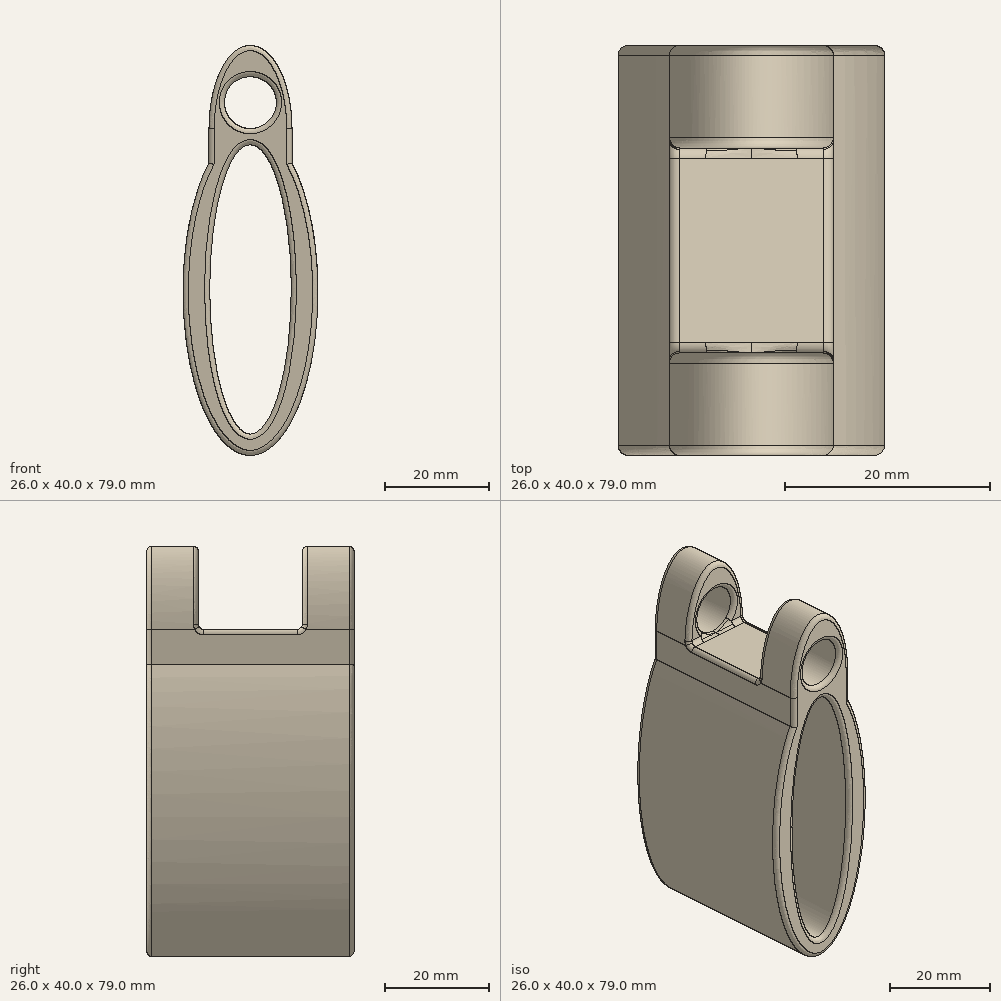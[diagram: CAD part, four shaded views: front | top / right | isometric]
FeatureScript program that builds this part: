
annotation { "Feature Type Name" : "Feature", "Feature Type Description" : "" }
export const myFeature = defineFeature(function(context is Context, id is Id, definition is map)
    precondition{}
    {
        {
            var Q0;
            Q0=qCreatedBy(makeId("Front.planeOp"),FACE);
            var sketch = newSketch(context, id + "F0", { "sketchPlane" : qUnion([Q0])});
            skEllipse(sketch, "E0", {"center": v(0, 0) * mm, "majorRadius": 28 * mm, "minorRadius": 8 * mm, "majorAxis": v(0, -1)});
            skLineSegment(sketch, "E1", {"start": v(0, 0) * mm, "end": v(8, 0) * mm, "construction": true});
            skLineSegment(sketch, "E2", {"start": v(0, 0) * mm, "end": v(0, 28) * mm, "construction": true});
            skLineSegment(sketch, "E3", {"start": v(-13, 0) * mm, "end": v(-8, 0) * mm, "construction": true});
            skLineSegment(sketch, "E4", {"start": v(0, 28) * mm, "end": v(0, 31) * mm, "construction": true});
            skLineSegment(sketch, "E5", {"start": v(0, 31) * mm, "end": v(0, 41) * mm, "construction": true});
            skPoint(sketch, "E6", {"position": v(0, 36) * mm});
            skCircle(sketch, "E7", {"center": v(0, 36) * mm, "radius": 5 * mm});
            skLineSegment(sketch, "E8", {"start": v(0, -28) * mm, "end": v(0, -32) * mm, "construction": true});
            skLineSegment(sketch, "E9.MirrorCS", {"start": v(8, 0) * mm, "end": v(8, 24.35) * mm, "construction": true});
            skPoint(sketch, "E10", {"position": v(0, 41) * mm});
            skLineSegment(sketch, "E11", {"start": v(0, 39) * mm, "end": v(0, 41) * mm, "construction": true});
            skLineSegment(sketch, "E12", {"start": v(8, 24.35) * mm, "end": v(8, 31) * mm});
            skLineSegment(sketch, "E13.MirrorCS", {"start": v(-8, 0) * mm, "end": v(-8, 24.35) * mm, "construction": true});
            skLineSegment(sketch, "E14.MirrorCS", {"start": v(-8, 24.35) * mm, "end": v(-8, 31) * mm});
            skEllipticalArc(sketch, "E15", {});
            skEllipticalArc(sketch, "E16", {});
            skLineSegment(sketch, "E17", {"start": v(8, 31) * mm, "end": v(-8, 31) * mm});
            const initialGuessF0  = {"E15": [0, -0.0004919260973110795, 0, -1, 0.03150807390268892, 0.013001584706273748, 3.804371322222278, 2.478813984957308], "E16": [0, 0.031, 0, -1, 0.016029827803373333, 0.008, 1.5707963267948966, 4.71238898038469]};
            skSetInitialGuess(sketch, initialGuessF0);
            skSolve(sketch);
        }
        {
            var Q0;
            Q0=makeQuery(id+"F0.imprint","IMPRINT",FACE,{"disambiguationData":[TD([[makeQuery(id+"F0.imprint","IMPRINT",EDGE,{"derivedFrom":sQuery(id+"F0.wireOp",EDGE,"E0")}),-1.0]])]});
            var Q1;
            Q1=makeQuery(id+"F0.imprint","IMPRINT",FACE,{"disambiguationData":[TD([[makeQuery(id+"F0.imprint","IMPRINT",EDGE,{"derivedFrom":sQuery(id+"F0.wireOp",EDGE,"E0")}),1.0]])]});
            extrude(context, id + "F1", {"entities" : qUnion([Q0, Q1]), "depth" : 40 * mm, "offsetDistance" : 25 * mm});
        }
        {
            var Q0;
            Q0=makeQuery(id+"F0.imprint","IMPRINT",FACE,{"disambiguationData":[TD([[makeQuery(id+"F0.imprint","IMPRINT",EDGE,{"derivedFrom":sQuery(id+"F0.wireOp",EDGE,"E0")}),1.0]])]});
            var Q1;
            Q1=makeQuery(id+"F1.opExtrude","CAP_FACE",FACE,{"disambiguationData":[OSD([sQuery(id+"F0.wireOp",EDGE,"E12"),sQuery(id+"F0.wireOp",EDGE,"E14.MirrorCS"),sQuery(id+"F0.wireOp",EDGE,"E15"),sQuery(id+"F0.wireOp",EDGE,"E17")])],"isStart":false});
            extrude(context, id + "F2", {"entities" : qUnion([Q0]), "operationType" : NewBodyOperationType.REMOVE, "endBound" : BoundingType.UP_TO_SURFACE, "depth" : 25 * mm, "endBoundEntityFace" : qUnion([Q1]), "offsetDistance" : 25 * mm, "hasDraft" : true, "draftAngle" : .2 * degree, "draftPullDirection" : true});
        }
        {
            var Q0;
            {var subQ0=sQuery(id+"F0.wireOp",EDGE,"E7");Q0=makeQuery(id+"F0.imprint","IMPRINT",FACE,{"disambiguationData":[TD([[makeQuery(id+"F0.imprint","IMPRINT",EDGE,{"derivedFrom":subQ0}),-1.0]])]});}
            var Q1;
            Q1=makeQuery(id+"F0.imprint","IMPRINT",FACE,{"disambiguationData":[TD([[makeQuery(id+"F0.imprint","IMPRINT",EDGE,{"derivedFrom":sQuery(id+"F0.wireOp",EDGE,"E7")}),1.0]])]});
            extrude(context, id + "F3", {"entities" : qUnion([Q0, Q1]), "operationType" : NewBodyOperationType.ADD, "depth" : 10 * mm, "offsetDistance" : 25 * mm});
        }
        {
            var Q0;
            Q0=makeQuery(id+"F0.imprint","IMPRINT",FACE,{"disambiguationData":[TD([[makeQuery(id+"F0.imprint","IMPRINT",EDGE,{"derivedFrom":sQuery(id+"F0.wireOp",EDGE,"E7")}),1.0]])]});
            extrude(context, id + "F4", {"entities" : qUnion([Q0]), "operationType" : NewBodyOperationType.REMOVE, "depth" : 10 * mm, "offsetDistance" : 25 * mm});
        }
        {
            var Q0;
            Q0=makeQuery(id+"F1.opExtrude","CAP_FACE",FACE,{"disambiguationData":[OSD([sQuery(id+"F0.wireOp",EDGE,"E12"),sQuery(id+"F0.wireOp",EDGE,"E14.MirrorCS"),sQuery(id+"F0.wireOp",EDGE,"E15"),sQuery(id+"F0.wireOp",EDGE,"E17")])],"isStart":false});
            cPlane(context, id + "F5", {"entities" : qUnion([Q0]), "cplaneType" : CPlaneType.OFFSET, "offset" : 0 * mm, "width" : 150 * mm, "height" : 150 * mm});
        }
        {
            var Q0;
            Q0=qCreatedBy(id+"F5.planeOp",FACE);
            var sketch = newSketch(context, id + "F6", { "sketchPlane" : qUnion([Q0])});
            skLineSegment(sketch, "E18", {"start": v(0, 31) * mm, "end": v(0, 41) * mm, "construction": true});
            skPoint(sketch, "E19", {"position": v(0, 36) * mm});
            skCircle(sketch, "E20", {"center": v(0, 36) * mm, "radius": 5 * mm});
            skPoint(sketch, "E21", {"position": v(0, 41) * mm});
            skLineSegment(sketch, "E22", {"start": v(0, 39) * mm, "end": v(0, 41) * mm, "construction": true});
            skEllipticalArc(sketch, "E23", {});
            skLineSegment(sketch, "E24", {"start": v(8, 31) * mm, "end": v(-8, 31) * mm});
            const initialGuessF6  = {"E23": [0, 0.031, 0, -1, 0.016029827803373333, 0.008, 1.5707963267948966, 4.71238898038469]};
            skSetInitialGuess(sketch, initialGuessF6);
            skSolve(sketch);
        }
        {
            var Q0;
            {var subQ0=sQuery(id+"F6.wireOp",EDGE,"E20");Q0=makeQuery(id+"F6.imprint","IMPRINT",FACE,{"disambiguationData":[TD([[makeQuery(id+"F6.imprint","IMPRINT",EDGE,{"derivedFrom":subQ0}),-1.0]])]});}
            var Q1;
            Q1=makeQuery(id+"F6.imprint","IMPRINT",FACE,{"disambiguationData":[TD([[makeQuery(id+"F6.imprint","IMPRINT",EDGE,{"derivedFrom":sQuery(id+"F6.wireOp",EDGE,"E20")}),1.0]])]});
            extrude(context, id + "F7", {"entities" : qUnion([Q0, Q1]), "operationType" : NewBodyOperationType.ADD, "oppositeDirection" : true, "depth" : 10 * mm, "offsetDistance" : 25 * mm});
        }
        {
            var Q0;
            Q0=makeQuery(id+"F6.imprint","IMPRINT",FACE,{"disambiguationData":[TD([[makeQuery(id+"F6.imprint","IMPRINT",EDGE,{"derivedFrom":sQuery(id+"F6.wireOp",EDGE,"E20")}),1.0]])]});
            extrude(context, id + "F8", {"entities" : qUnion([Q0]), "operationType" : NewBodyOperationType.REMOVE, "oppositeDirection" : true, "depth" : 10 * mm, "offsetDistance" : 25 * mm});
        }
        {
            var Q0;
            {var subQ0=sQuery(id+"F0.wireOp",EDGE,"E17");Q0=makeQuery(id+"F3.boolean.opBoolean","MERGE",FACE,{"derivedFrom":[makeQuery(id+"F1.opExtrude","CAP_FACE",FACE,{"disambiguationData":[OSD([sQuery(id+"F0.wireOp",EDGE,"E12"),sQuery(id+"F0.wireOp",EDGE,"E14.MirrorCS"),sQuery(id+"F0.wireOp",EDGE,"E15"),subQ0])],"isStart":true}),makeQuery(id+"F3.opExtrude","CAP_FACE",FACE,{"disambiguationData":[OSD([sQuery(id+"F0.wireOp",EDGE,"E16"),subQ0])],"isStart":true})]});}
            fillet(context, id + "F9", {"entities" : qUnion([Q0]), "radius" : 1 * mm, "tangentPropagation" : true, "allowEdgeOverflow" : false});
        }
        {
            var Q0;
            Q0=makeQuery(id+"F7.boolean.opBoolean","MERGE",FACE,{"derivedFrom":[makeQuery(id+"F1.opExtrude","CAP_FACE",FACE,{"disambiguationData":[OSD([sQuery(id+"F0.wireOp",EDGE,"E12"),sQuery(id+"F0.wireOp",EDGE,"E14.MirrorCS"),sQuery(id+"F0.wireOp",EDGE,"E15"),sQuery(id+"F0.wireOp",EDGE,"E17")])],"isStart":false}),makeQuery(id+"F7.opExtrude","CAP_FACE",FACE,{"disambiguationData":[OSD([sQuery(id+"F6.wireOp",EDGE,"E23"),sQuery(id+"F6.wireOp",EDGE,"E24")])],"isStart":true})]});
            fillet(context, id + "F10", {"entities" : qUnion([Q0]), "radius" : 1 * mm, "tangentPropagation" : true, "allowEdgeOverflow" : false});
        }
        {
            var Q0;
            Q0=makeQuery(id+"F7.opExtrude","CAP_FACE",FACE,{"disambiguationData":[OSD([sQuery(id+"F6.wireOp",EDGE,"E23"),sQuery(id+"F6.wireOp",EDGE,"E24")])],"isStart":false});
            var Q1;
            Q1=makeQuery(id+"F1.opExtrude","SWEPT_FACE",FACE,{"disambiguationData":[OSD([sQuery(id+"F0.wireOp",EDGE,"E17")])]});
            var Q2;
            Q2=makeQuery(id+"F3.opExtrude","CAP_FACE",FACE,{"disambiguationData":[OSD([sQuery(id+"F0.wireOp",EDGE,"E16"),sQuery(id+"F0.wireOp",EDGE,"E17")])],"isStart":false});
            fillet(context, id + "F11", {"entities" : qUnion([Q0, Q1, Q2]), "radius" : 1 * mm, "tangentPropagation" : true, "allowEdgeOverflow" : false});
        }
    });
